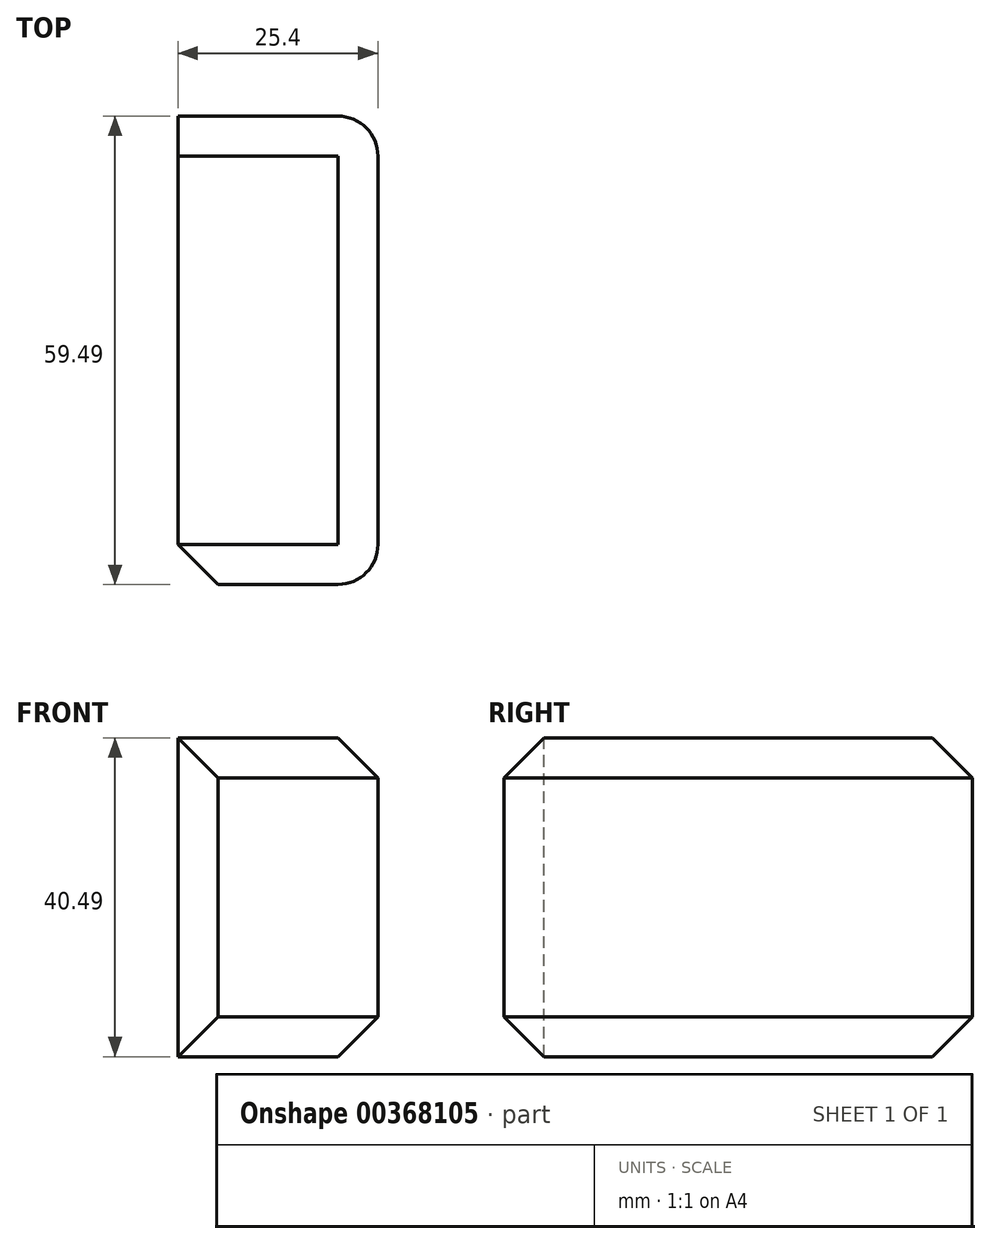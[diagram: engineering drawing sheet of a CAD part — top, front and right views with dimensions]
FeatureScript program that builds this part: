
annotation { "Feature Type Name" : "Feature", "Feature Type Description" : "" }
export const myFeature = defineFeature(function(context is Context, id is Id, definition is map)
    precondition{}
    {
        {
            var Q0;
            Q0=qCreatedBy(makeId("Right.planeOp"),FACE);
            var sketch = newSketch(context, id + "F0", { "sketchPlane" : qUnion([Q0])});
            skLineSegment(sketch, "E0.bottom", {"start": v(-27.5, -17.99) * mm, "end": v(31.99, -17.99) * mm});
            skLineSegment(sketch, "E0.top", {"start": v(-27.5, 22.5) * mm, "end": v(31.99, 22.5) * mm});
            skLineSegment(sketch, "E0.left", {"start": v(-27.5, -17.99) * mm, "end": v(-27.5, 22.5) * mm});
            skLineSegment(sketch, "E0.right", {"start": v(31.99, -17.99) * mm, "end": v(31.99, 22.5) * mm});
            skSolve(sketch);
        }
        {
            var Q0;
            Q0 = qSketchRegion(id + "F0", true);
            extrude(context, id + "F1", {"entities" : qUnion([Q0]), "depth" : 25.4 * mm});
        }
        {
            var Q0;
            Q0=makeQuery(id+"F1.opExtrude","CAP_EDGE",EDGE,{"disambiguationData":[OSD([sQuery(id+"F0.wireOp",EDGE,"E0.left")])],"isStart":false});
            var Q1;
            Q1=makeQuery(id+"F1.opExtrude","CAP_EDGE",EDGE,{"disambiguationData":[OSD([sQuery(id+"F0.wireOp",EDGE,"E0.right")])],"isStart":false});
            fillet(context, id + "F2", {"entities" : qUnion([Q0, Q1]), "radius" : 5.08 * mm, "tangentPropagation" : true, "allowEdgeOverflow" : false});
        }
        {
            var Q0;
            Q0=makeQuery(id+"F1.opExtrude","SWEPT_FACE",FACE,{"disambiguationData":[OSD([sQuery(id+"F0.wireOp",EDGE,"E0.left")])]});
            chamfer(context, id + "F3", {"entities" : qUnion([Q0]), "width" : 5.08 * mm, "tangentPropagation" : true});
        }
    });
